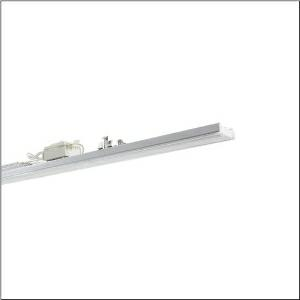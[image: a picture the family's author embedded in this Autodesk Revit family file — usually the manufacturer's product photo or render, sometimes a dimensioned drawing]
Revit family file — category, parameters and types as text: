
# Revit family: licross_r__21_recessed_mo_51te11vn465g_bbcd
name_source: partatom
category: Lighting Fixtures
units: mm (PartAtom-declared; Revit-internal decimal feet)

## family parameters
Cut with Voids When Loaded = No
Host = Face
Light Source = No
Part Type = Normal
Room Calculation Point = No
Round Connector Dimension = Use Diameter
Shared = No

## types (1)
- --- (1 x LED, 6500 lm, 34.8 W, 4000K)
    Apparent Load = 35 VA
    CIE Flux Codes = 89 96 99 100 100
    Color Rendering = 80
    Color Temperature = 4000K
    Default Elevation = 1800 mm
    Description = Licross® 21 Recessed MO, luminaire insert, of sheet steel, galvanised, coil coated, white, length: 1.500mm, width: 66mm, height: 67mm, LED rated luminous flux: 6.500lm, light colour: 840, control gear: DALI 2, CLO, with plug, 5-pole, with phase selection, mains connection: 220..240V, AC, 50/60Hz, start of lifetime: 35W, end of service life: 38W, internal wiring halogen-free, primary light control with lens, of plastic, primary optical cover: cover, of PMMA, light emission: direct distribution, primary light characteristic: symmetric, protection rating (complete): IP54, insulation class (complete): insulation class I (protective earthing), certification: CE, ENEC, VDE, UKCA, protection symbol: D if used in an environment with non-conductive dust loads with corresponding accessories, impact resistance: IK06, permissible ambient temperature for indoor applications: -25..+40°C, corresponds to IFS (International Featured Standards) requirements for safety and quality in the food industry, reducing of maximum allowable ambient temperature of 5°C with ceiling mounting, LABS conformity tested according to VDMA 24364:2018-05, packaging unit: 1 piece
    Height = 58 mm
    Lamp = 1 x LED
    Lamp Light Flux = 6500 lm
    Lamp Power = 34.8 W
    Lamp count = 1
    Length = 1500 mm
    Luminous efficacy = 187 lm/W
    Manufacturer = Siteco
    ModVariant = No
    Model = 51TE11VN465G
    Mounting Place = Ceiling
    Mounting Type = Pendant
    Number of Poles = 1
    OnlyDefault = Yes
    Power Factor = 1
    Product Name = Licross® 21 Recessed MO
    Product group = luminaire insert | ceiling pendant
    ProductGroupID = 902
    Protection Class = Protection class I
    Protection Degree = IP 54
    RLX_Detail_Level = 1
    RLX_Emergency_Light_Flux = 0 lm
    RLX_Emergency_Type = 0
    RLX_Emergency_Type_DB = No
    RlxData = <blob elided: 24377 chars, md5=ade7bab3>
    Socket = socket
    Standby Power = 0 W
    System Light Flux = 6500 lm
    System Power = 35 W
    Type Comments = factory setting: luminous flux: 100 % | dim-lin: 254 | 236 mA
    Type Image = l_1296930.jpg
    URL = http://relux.com
    VarID = @adj_108451
    Voltage = 0 V
    Weight = 0.00 kg
    Width = 66 mm

## geometry (parser evidence)
native form markers: Blend x4, Sweep x11
no freeform markers — native parametric forms only
